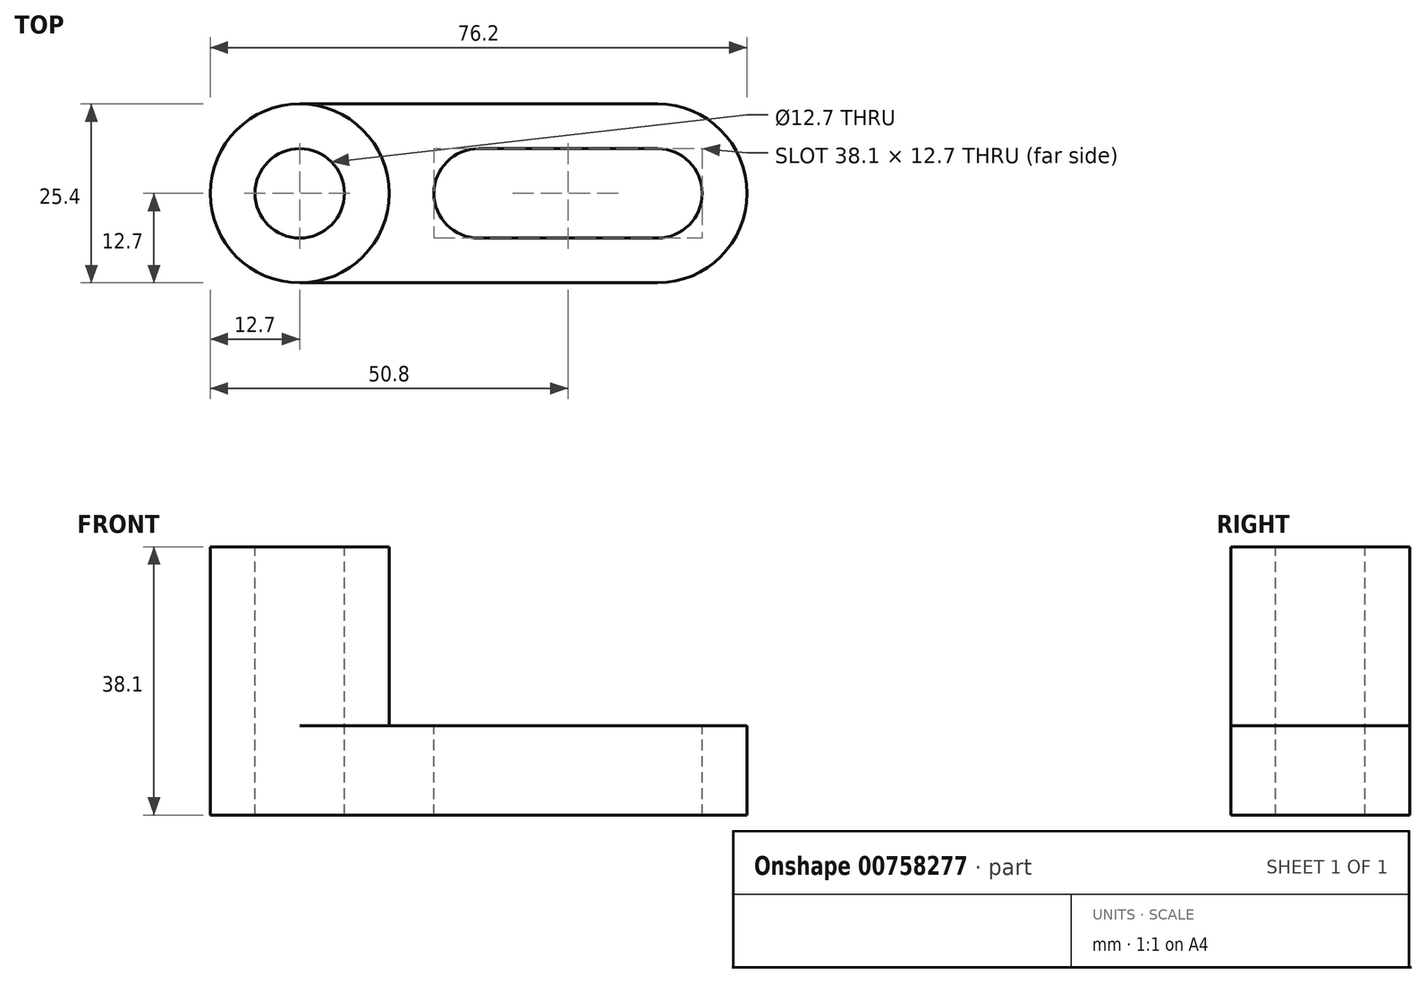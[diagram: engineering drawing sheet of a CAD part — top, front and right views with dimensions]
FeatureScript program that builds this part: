
annotation { "Feature Type Name" : "Feature", "Feature Type Description" : "" }
export const myFeature = defineFeature(function(context is Context, id is Id, definition is map)
    precondition{}
    {
        {
            var Q0;
            Q0=qCreatedBy(makeId("Front.planeOp"),FACE);
            var sketch = newSketch(context, id + "F0", { "sketchPlane" : qUnion([Q0])});
            skLineSegment(sketch, "E0", {"start": v(0, 0) * mm, "end": v(76.2, 0) * mm});
            skLineSegment(sketch, "E1", {"start": v(76.2, 0) * mm, "end": v(76.2, 38.1) * mm});
            skLineSegment(sketch, "E2", {"start": v(76.2, 38.1) * mm, "end": v(0, 38.1) * mm});
            skLineSegment(sketch, "E3", {"start": v(0, 38.1) * mm, "end": v(0, 0) * mm});
            skSolve(sketch);
        }
        {
            var Q0;
            Q0=makeQuery(id+"F0.imprint","IMPRINT",FACE,{"disambiguationData":[TD([[makeQuery(id+"F0.imprint","IMPRINT",EDGE,{"derivedFrom":sQuery(id+"F0.wireOp",EDGE,"E0")}),1.0]])]});
            extrude(context, id + "F1", {"entities" : qUnion([Q0]), "depth" : 25.4 * mm, "offsetDistance" : 25.4 * mm});
        }
        {
            var Q0;
            Q0=makeQuery(id+"F1.opExtrude","SWEPT_FACE",FACE,{"disambiguationData":[OSD([sQuery(id+"F0.wireOp",EDGE,"E2")])]});
            var sketch = newSketch(context, id + "F2", { "sketchPlane" : qUnion([Q0])});
            skCircle(sketch, "E4", {"center": v(12.7, -12.7) * mm, "radius": 12.7 * mm});
            skCircle(sketch, "E5", {"center": v(12.7, -12.7) * mm, "radius": 6.35 * mm});
            skSolve(sketch);
        }
        {
            var Q0;
            {var subQ0=sQuery(id+"F2.wireOp",EDGE,"E4");var subQ1=sQuery(id+"F0.wireOp",EDGE,"E2");var subQ4=makeQuery(id+"F1.opExtrude","CAP_EDGE",EDGE,{"disambiguationData":[OSD([subQ1])],"isStart":false});var subQ5=makeQuery(id+"F2.imprint","INTERSECT",VERTEX,{"derivedFrom":[subQ4,subQ0]});Q0=makeQuery(id+"F2.imprint","IMPRINT",FACE,{"disambiguationData":[TD([[makeQuery(id+"F2.imprint","IMPRINT",EDGE,{"disambiguationData":[TD([[subQ5,1.0]])],"derivedFrom":subQ0}),-1.0]])]});}
            var Q1;
            {var subQ0=sQuery(id+"F2.wireOp",EDGE,"E4");var subQ1=sQuery(id+"F0.wireOp",EDGE,"E2");var subQ4=makeQuery(id+"F1.opExtrude","CAP_EDGE",EDGE,{"disambiguationData":[OSD([subQ1])],"isStart":true});var subQ5=makeQuery(id+"F2.imprint","INTERSECT",VERTEX,{"derivedFrom":[subQ4,subQ0]});Q1=makeQuery(id+"F2.imprint","IMPRINT",FACE,{"disambiguationData":[TD([[makeQuery(id+"F2.imprint","IMPRINT",EDGE,{"disambiguationData":[TD([[subQ5,-1.0]])],"derivedFrom":subQ0}),-1.0]])]});}
            var Q2;
            Q2=makeQuery(id+"F2.imprint","IMPRINT",FACE,{"disambiguationData":[TD([[makeQuery(id+"F2.imprint","IMPRINT",EDGE,{"derivedFrom":sQuery(id+"F2.wireOp",EDGE,"E5")}),1.0]])]});
            var Q3;
            {var subQ1=sQuery(id+"F0.wireOp",EDGE,"E2");var subQ6=makeQuery(id+"F1.opExtrude","SWEPT_EDGE",EDGE,{"disambiguationData":[OSD([sQuery(id+"F0.wireOp",EDGE,"E1"),subQ1])]});Q3=makeQuery(id+"F2.imprint","IMPRINT",FACE,{"disambiguationData":[TD([[makeQuery(id+"F2.imprint","IMPRINT",EDGE,{"derivedFrom":subQ6}),1.0]])]});}
            extrude(context, id + "F3", {"entities" : qUnion([Q0, Q1, Q2, Q3]), "operationType" : NewBodyOperationType.REMOVE, "oppositeDirection" : true, "depth" : 25.4 * mm, "offsetDistance" : 25.4 * mm});
        }
        {
            var Q0;
            {var subQ0=sQuery(id+"F0.wireOp",EDGE,"E2");var subQ1=makeQuery(id+"F1.opExtrude","CAP_EDGE",EDGE,{"disambiguationData":[OSD([subQ0])],"isStart":true});var subQ2=sQuery(id+"F0.wireOp",EDGE,"E3");var subQ3=makeQuery(id+"F1.opExtrude","SWEPT_EDGE",EDGE,{"disambiguationData":[OSD([subQ0,subQ2])]});var subQ4=makeQuery(id+"F2.imprint","INTERSECT",VERTEX,{"derivedFrom":[subQ3,subQ1]});var subQ5=sQuery(id+"F2.wireOp",EDGE,"E4");var subQ6=makeQuery(id+"F2.imprint","INTERSECT",VERTEX,{"derivedFrom":[subQ1,subQ5]});Q0=makeQuery(id+"F3.boolean.opBoolean","COPY",FACE,{"derivedFrom":makeQuery(id+"F3.opExtrude","CAP_FACE",FACE,{"disambiguationData":[OSD([subQ0,subQ2,subQ5]),TDD([makeQuery(id+"F2.imprint","IMPRINT",EDGE,{"disambiguationData":[TD([[subQ6,-1.0]])],"derivedFrom":subQ5}),makeQuery(id+"F2.imprint","IMPRINT",EDGE,{"disambiguationData":[TD([[subQ4,1.0]])],"derivedFrom":subQ3}),makeQuery(id+"F2.imprint","IMPRINT",EDGE,{"disambiguationData":[TD([[subQ6,-1.0]])],"derivedFrom":subQ1})])],"isStart":false})});}
            var Q1;
            Q1=makeQuery(id+"F3.boolean.opBoolean","COPY",FACE,{"derivedFrom":makeQuery(id+"F3.opExtrude","CAP_FACE",FACE,{"disambiguationData":[OSD([sQuery(id+"F2.wireOp",EDGE,"E5")])],"isStart":false})});
            var Q2;
            {var subQ0=sQuery(id+"F0.wireOp",EDGE,"E2");var subQ1=makeQuery(id+"F1.opExtrude","CAP_EDGE",EDGE,{"disambiguationData":[OSD([subQ0])],"isStart":false});var subQ2=sQuery(id+"F0.wireOp",EDGE,"E3");var subQ3=makeQuery(id+"F1.opExtrude","SWEPT_EDGE",EDGE,{"disambiguationData":[OSD([subQ0,subQ2])]});var subQ4=makeQuery(id+"F2.imprint","INTERSECT",VERTEX,{"derivedFrom":[subQ3,subQ1]});var subQ5=sQuery(id+"F2.wireOp",EDGE,"E4");var subQ6=makeQuery(id+"F2.imprint","INTERSECT",VERTEX,{"derivedFrom":[subQ1,subQ5]});Q2=makeQuery(id+"F3.boolean.opBoolean","COPY",FACE,{"derivedFrom":makeQuery(id+"F3.opExtrude","CAP_FACE",FACE,{"disambiguationData":[OSD([subQ0,subQ2,subQ5]),TDD([makeQuery(id+"F2.imprint","IMPRINT",EDGE,{"disambiguationData":[TD([[subQ6,1.0]])],"derivedFrom":subQ5}),makeQuery(id+"F2.imprint","IMPRINT",EDGE,{"disambiguationData":[TD([[subQ4,-1.0]])],"derivedFrom":subQ3}),makeQuery(id+"F2.imprint","IMPRINT",EDGE,{"disambiguationData":[TD([[subQ6,-1.0]])],"derivedFrom":subQ1})])],"isStart":false})});}
            extrude(context, id + "F4", {"entities" : qUnion([Q0, Q1, Q2]), "operationType" : NewBodyOperationType.REMOVE, "oppositeDirection" : true, "depth" : 25.4 * mm, "offsetDistance" : 25.4 * mm});
        }
        {
            var Q0;
            Q0=makeQuery(id+"F3.boolean.opBoolean","COPY",FACE,{"derivedFrom":makeQuery(id+"F3.opExtrude","CAP_FACE",FACE,{"disambiguationData":[OSD([sQuery(id+"F0.wireOp",EDGE,"E1"),sQuery(id+"F0.wireOp",EDGE,"E2"),sQuery(id+"F2.wireOp",EDGE,"E4")])],"isStart":false})});
            var sketch = newSketch(context, id + "F5", { "sketchPlane" : qUnion([Q0])});
            skCircle(sketch, "E6", {"center": v(38.1, -12.7) * mm, "radius": 6.35 * mm});
            skCircle(sketch, "E7", {"center": v(63.5, -12.7) * mm, "radius": 6.35 * mm});
            skLineSegment(sketch, "E8", {"start": v(38.1, -6.35) * mm, "end": v(63.5, -6.35) * mm});
            skLineSegment(sketch, "E9", {"start": v(63.5, -19.05) * mm, "end": v(38.1, -19.05) * mm});
            skSolve(sketch);
        }
        {
            var Q0;
            {var subQ0=sQuery(id+"F5.wireOp",EDGE,"E6");var subQ1=makeQuery(id+"F5.imprint","INTERSECT",VERTEX,{"derivedFrom":[subQ0,sQuery(id+"F5.wireOp",EDGE,"E8")]});Q0=makeQuery(id+"F5.imprint","IMPRINT",FACE,{"disambiguationData":[TD([[makeQuery(id+"F5.imprint","IMPRINT",EDGE,{"disambiguationData":[TD([[subQ1,-1.0]])],"derivedFrom":subQ0}),1.0]])]});}
            var Q1;
            {var subQ0=sQuery(id+"F5.wireOp",EDGE,"E8");Q1=makeQuery(id+"F5.imprint","IMPRINT",FACE,{"disambiguationData":[TD([[makeQuery(id+"F5.imprint","IMPRINT",EDGE,{"derivedFrom":subQ0}),-1.0]])]});}
            var Q2;
            {var subQ0=sQuery(id+"F5.wireOp",EDGE,"E7");var subQ1=makeQuery(id+"F5.imprint","INTERSECT",VERTEX,{"derivedFrom":[subQ0,sQuery(id+"F5.wireOp",EDGE,"E8")]});Q2=makeQuery(id+"F5.imprint","IMPRINT",FACE,{"disambiguationData":[TD([[makeQuery(id+"F5.imprint","IMPRINT",EDGE,{"disambiguationData":[TD([[subQ1,-1.0]])],"derivedFrom":subQ0}),1.0]])]});}
            extrude(context, id + "F6", {"entities" : qUnion([Q0, Q1, Q2]), "operationType" : NewBodyOperationType.REMOVE, "oppositeDirection" : true, "depth" : 25.4 * mm, "offsetDistance" : 25.4 * mm});
        }
        {
            var Q0;
            Q0=makeQuery(id+"F3.boolean.opBoolean","COPY",FACE,{"derivedFrom":makeQuery(id+"F3.opExtrude","CAP_FACE",FACE,{"disambiguationData":[OSD([sQuery(id+"F0.wireOp",EDGE,"E1"),sQuery(id+"F0.wireOp",EDGE,"E2"),sQuery(id+"F2.wireOp",EDGE,"E4")])],"isStart":false})});
            var sketch = newSketch(context, id + "F7", { "sketchPlane" : qUnion([Q0])});
            skArc(sketch, "E10", {"start": v(63.5, -25.4) * mm, "mid": v(76.2, -12.7) * mm, "end": v(63.5, 0) * mm});
            skSolve(sketch);
        }
        {
            var Q0;
            {var subQ0=sQuery(id+"F7.wireOp",EDGE,"E10");var subQ1=sQuery(id+"F0.wireOp",EDGE,"E2");var subQ3=sQuery(id+"F0.wireOp",EDGE,"E1");var subQ6=makeQuery(id+"F3.boolean.opBoolean","COPY",EDGE,{"derivedFrom":makeQuery(id+"F3.opExtrude","CAP_EDGE",EDGE,{"disambiguationData":[OSD([subQ3,subQ1])],"isStart":false})});var subQ7=makeQuery(id+"F7.imprint","INTERSECT",VERTEX,{"derivedFrom":[subQ6,subQ0]});Q0=makeQuery(id+"F7.imprint","IMPRINT",FACE,{"disambiguationData":[TD([[makeQuery(id+"F7.imprint","IMPRINT",EDGE,{"disambiguationData":[TD([[subQ7,-1.0]])],"derivedFrom":subQ0}),-1.0]])]});}
            var Q1;
            {var subQ0=sQuery(id+"F7.wireOp",EDGE,"E10");var subQ1=sQuery(id+"F0.wireOp",EDGE,"E2");var subQ3=sQuery(id+"F0.wireOp",EDGE,"E1");var subQ6=makeQuery(id+"F3.boolean.opBoolean","COPY",EDGE,{"derivedFrom":makeQuery(id+"F3.opExtrude","CAP_EDGE",EDGE,{"disambiguationData":[OSD([subQ3,subQ1])],"isStart":false})});var subQ7=makeQuery(id+"F7.imprint","INTERSECT",VERTEX,{"derivedFrom":[subQ6,subQ0]});Q1=makeQuery(id+"F7.imprint","IMPRINT",FACE,{"disambiguationData":[TD([[makeQuery(id+"F7.imprint","IMPRINT",EDGE,{"disambiguationData":[TD([[subQ7,1.0]])],"derivedFrom":subQ0}),-1.0]])]});}
            extrude(context, id + "F8", {"entities" : qUnion([Q0, Q1]), "operationType" : NewBodyOperationType.REMOVE, "oppositeDirection" : true, "depth" : 25.4 * mm, "offsetDistance" : 25.4 * mm});
        }
    });
